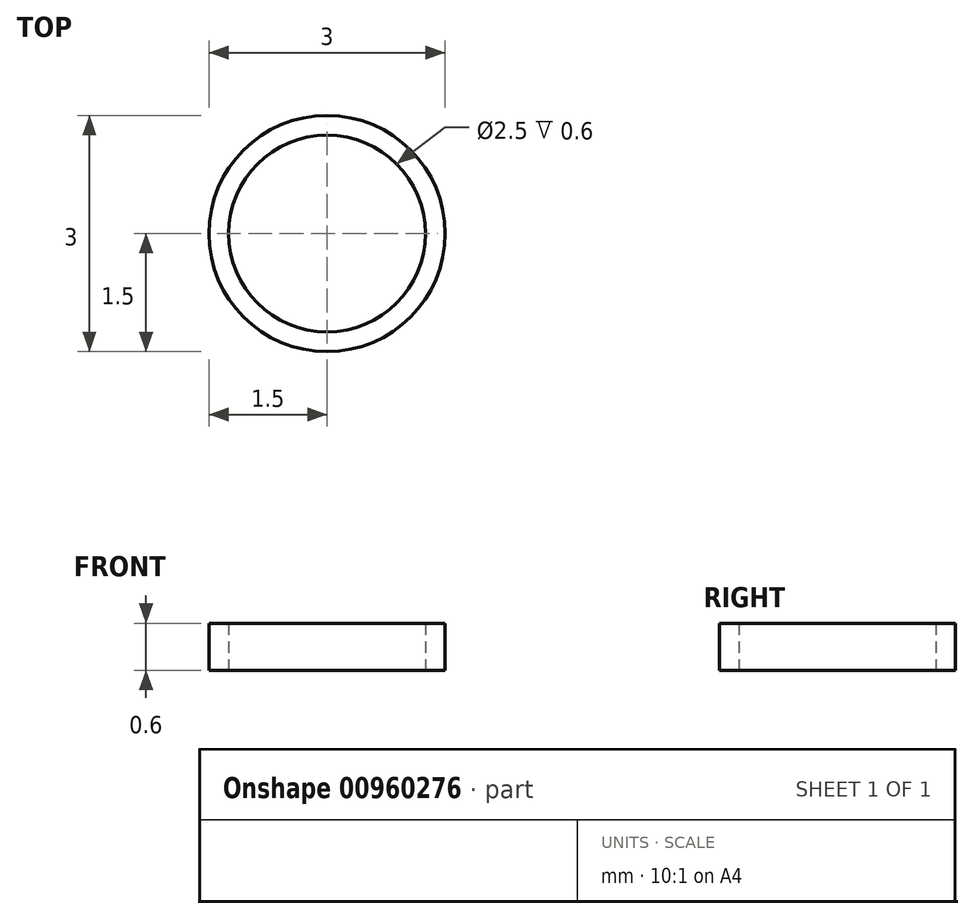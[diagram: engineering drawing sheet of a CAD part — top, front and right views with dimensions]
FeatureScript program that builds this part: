
annotation { "Feature Type Name" : "Feature", "Feature Type Description" : "" }
export const myFeature = defineFeature(function(context is Context, id is Id, definition is map)
    precondition{}
    {
        {
            var Q0;
            Q0=qCreatedBy(makeId("Top.planeOp"),FACE);
            var sketch = newSketch(context, id + "F0", { "sketchPlane" : qUnion([Q0])});
            skCircle(sketch, "E0", {"center": v(0, 0) * mm, "radius": 1.5 * mm});
            skSolve(sketch);
        }
        {
            var Q0;
            Q0 = qSketchRegion(id + "F0", true);
            extrude(context, id + "F1", {"entities" : qUnion([Q0]), "depth" : 0.6 * mm, "offsetDistance" : 25 * mm});
        }
        {
            var Q0;
            Q0=sQuery(id+"F0.wireOp",VERTEX,"E0.center");
            var Q1;
            Q1=makeQuery(id+"F1.opExtrude","SWEPT_BODY",BODY,{"disambiguationData":[OSD([sQuery(id+"F0.wireOp",EDGE,"E0")])]});
            hole(context, id + "F2", {"style" : HoleStyle.SIMPLE, "endStyle" : HoleEndStyle.THROUGH, "oppositeDirection" : true, "standardTappedOrClearance" : lookupTablePath({ "standard" : "ISO", "engagement" : "75%", "pitch" : "0.5 mm", "size" : "M3", "type" : "Tapped" }), "standardBlindInLast" : lookupTablePath({ "standard" : "ISO", "fit" : "Normal", "engagement" : "75%", "pitch" : "0.5 mm", "size" : "M3", "type" : "Clearance & tapped" }), "holeDiameter" : 2.5 * mm, "majorDiameter" : 3 * mm, "showTappedDepth" : true, "isTappedThrough" : true, "tappedDepth" : 1.2 * mm, "tapClearance" : 3, "startFromSketch" : true, "locations" : qUnion([Q0]), "scope" : qUnion([Q1])});
        }
    });
